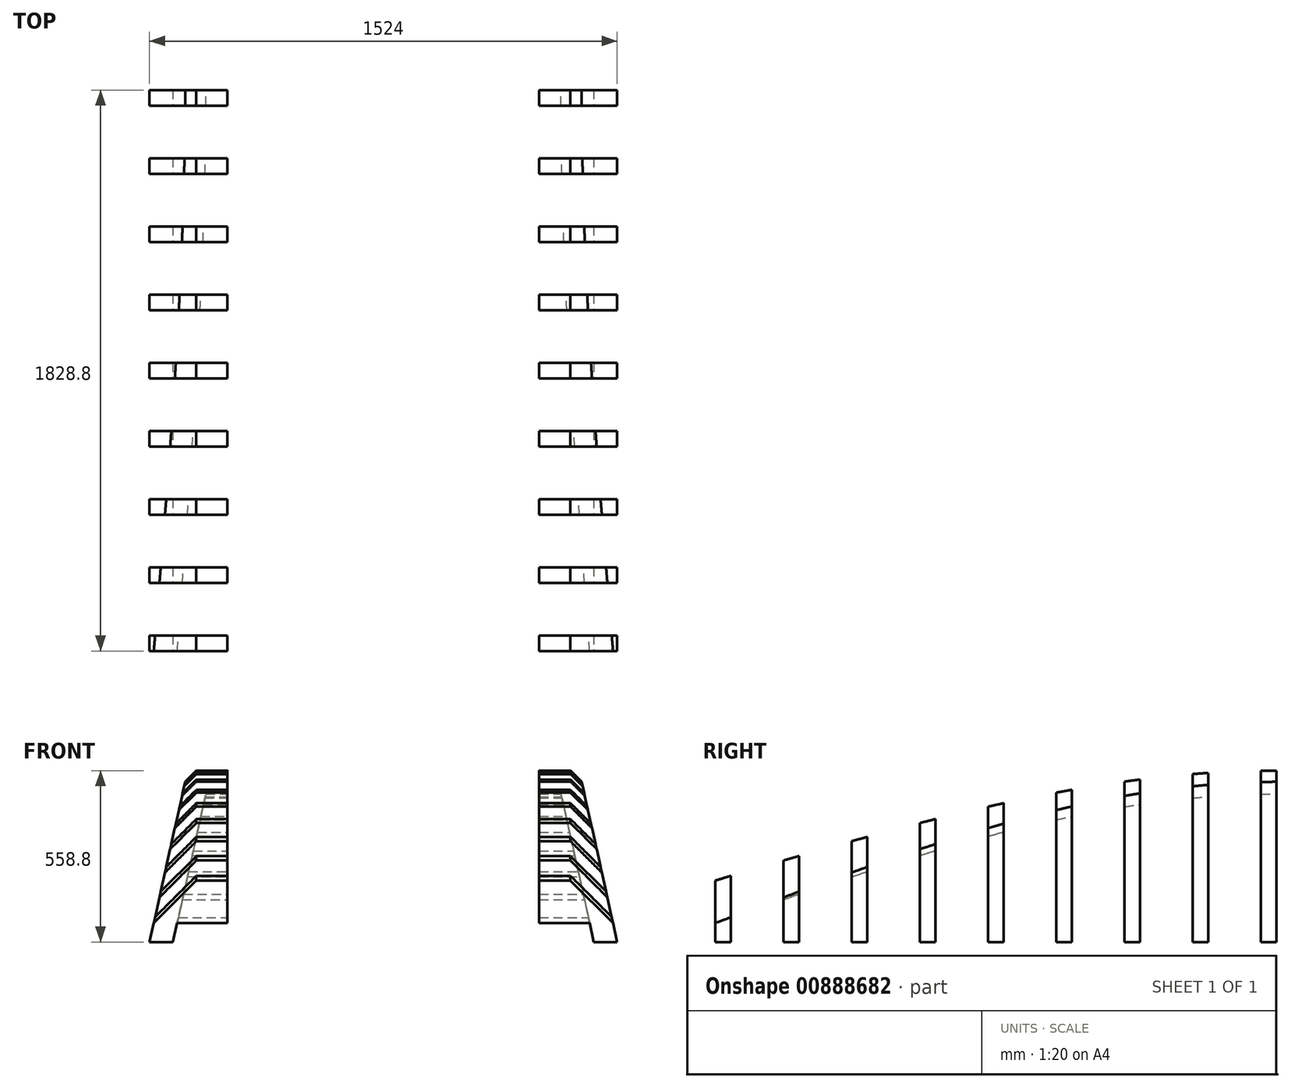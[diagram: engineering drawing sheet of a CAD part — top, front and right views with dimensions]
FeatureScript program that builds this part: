
annotation { "Feature Type Name" : "Feature", "Feature Type Description" : "" }
export const myFeature = defineFeature(function(context is Context, id is Id, definition is map)
    precondition{}
    {
        {
            var Q0;
            Q0=qCreatedBy(makeId("Front.planeOp"),FACE);
            var sketch = newSketch(context, id + "F0", { "sketchPlane" : qUnion([Q0])});
            skLineSegment(sketch, "E0", {"start": v(762, 0) * mm, "end": v(646.24, 522.16) * mm});
            skLineSegment(sketch, "E1", {"start": v(646.24, 522.16) * mm, "end": v(609.6, 558.8) * mm});
            skLineSegment(sketch, "E2", {"start": v(609.6, 558.8) * mm, "end": v(0, 558.8) * mm});
            skLineSegment(sketch, "E3", {"start": v(762, 0) * mm, "end": v(685.8, 0) * mm});
            skLineSegment(sketch, "E4", {"start": v(685.8, 0) * mm, "end": v(578.81, 482.6) * mm});
            skLineSegment(sketch, "E5", {"start": v(578.81, 482.6) * mm, "end": v(0, 482.6) * mm});
            skLineSegment(sketch, "E6", {"start": v(0, 558.8) * mm, "end": v(0, 482.6) * mm, "construction": true});
            skLineSegment(sketch, "E7.MirrorCS", {"start": v(-762, 0) * mm, "end": v(-685.8, 0) * mm});
            skLineSegment(sketch, "E8.MirrorCS", {"start": v(-646.24, 522.16) * mm, "end": v(-609.6, 558.8) * mm});
            skLineSegment(sketch, "E9.MirrorCS", {"start": v(-762, 0) * mm, "end": v(-646.24, 522.16) * mm});
            skLineSegment(sketch, "E10.MirrorCS", {"start": v(-685.8, 0) * mm, "end": v(-578.81, 482.6) * mm});
            skLineSegment(sketch, "E11.MirrorCS", {"start": v(-578.81, 482.6) * mm, "end": v(0, 482.6) * mm});
            skLineSegment(sketch, "E12.MirrorCS", {"start": v(-609.6, 558.8) * mm, "end": v(0, 558.8) * mm});
            skSolve(sketch);
        }
        {
            var Q0;
            Q0=qCreatedBy(makeId("Front.planeOp"),FACE);
            cPlane(context, id + "F1", {"entities" : qUnion([Q0]), "cplaneType" : CPlaneType.OFFSET, "offset" : 1828.8 * mm, "width" : 152.4 * mm, "height" : 152.4 * mm});
        }
        {
            var Q0;
            Q0=qCreatedBy(id+"F1.planeOp",FACE);
            var sketch = newSketch(context, id + "F2", { "sketchPlane" : qUnion([Q0])});
            skLineSegment(sketch, "E13", {"start": v(762, 0) * mm, "end": v(748.26, 62) * mm});
            skLineSegment(sketch, "E14", {"start": v(748.26, 62) * mm, "end": v(609.6, 200.65) * mm});
            skLineSegment(sketch, "E15", {"start": v(609.6, 200.65) * mm, "end": v(0, 200.65) * mm});
            skLineSegment(sketch, "E16", {"start": v(762, 0) * mm, "end": v(685.8, 0) * mm});
            skLineSegment(sketch, "E17", {"start": v(685.8, 0) * mm, "end": v(672.06, 62) * mm});
            skLineSegment(sketch, "E18", {"start": v(672.06, 62) * mm, "end": v(0, 62) * mm});
            skLineSegment(sketch, "E19", {"start": v(0, 62) * mm, "end": v(0, 200.65) * mm, "construction": true});
            skLineSegment(sketch, "E20.MirrorCS", {"start": v(-672.06, 62) * mm, "end": v(0, 62) * mm});
            skLineSegment(sketch, "E21.MirrorCS", {"start": v(-685.8, 0) * mm, "end": v(-672.06, 62) * mm});
            skLineSegment(sketch, "E22.MirrorCS", {"start": v(-609.6, 200.65) * mm, "end": v(0, 200.65) * mm});
            skLineSegment(sketch, "E23.MirrorCS", {"start": v(-748.26, 62) * mm, "end": v(-609.6, 200.65) * mm});
            skLineSegment(sketch, "E24.MirrorCS", {"start": v(-762, 0) * mm, "end": v(-685.8, 0) * mm});
            skLineSegment(sketch, "E25.MirrorCS", {"start": v(-762, 0) * mm, "end": v(-748.26, 62) * mm});
            skSolve(sketch);
        }
        {
            var Q0;
            Q0=makeQuery(id+"F0.imprint","IMPRINT",FACE,{"disambiguationData":[TD([[makeQuery(id+"F0.imprint","IMPRINT",EDGE,{"derivedFrom":sQuery(id+"F0.wireOp",EDGE,"E0")}),1.0]])]});
            var Q1;
            Q1=makeQuery(id+"F2.imprint","IMPRINT",FACE,{"disambiguationData":[TD([[makeQuery(id+"F2.imprint","IMPRINT",EDGE,{"derivedFrom":sQuery(id+"F2.wireOp",EDGE,"E13")}),1.0]])]});
            loft(context, id + "F3", {"sheetProfilesArray" : [{ "sheetProfileEntities" : qUnion([Q0]) }, { "sheetProfileEntities" : qUnion([Q1]) }], "startCondition" : LoftEndDerivativeType.NORMAL_TO_PROFILE, "startMagnitude" : 1});
        }
        {
            var Q0;
            Q0=qCreatedBy(makeId("Right.planeOp"),FACE);
            var sketch = newSketch(context, id + "F4", { "sketchPlane" : qUnion([Q0])});
            skLineSegment(sketch, "E26.bottom", {"start": v(-50.8, 0) * mm, "end": v(-222.25, 0) * mm});
            skLineSegment(sketch, "E26.top", {"start": v(-50.8, 609.6) * mm, "end": v(-222.25, 609.6) * mm});
            skLineSegment(sketch, "E26.left", {"start": v(-50.8, 0) * mm, "end": v(-50.8, 609.6) * mm});
            skLineSegment(sketch, "E26.right", {"start": v(-222.25, 0) * mm, "end": v(-222.25, 609.6) * mm});
            skLineSegment(sketch, "E27.bottom", {"start": v(-273.05, 0) * mm, "end": v(-444.5, 0) * mm});
            skLineSegment(sketch, "E27.top", {"start": v(-273.05, 609.6) * mm, "end": v(-444.5, 609.6) * mm});
            skLineSegment(sketch, "E27.left", {"start": v(-273.05, 0) * mm, "end": v(-273.05, 609.6) * mm});
            skLineSegment(sketch, "E27.right", {"start": v(-444.5, 0) * mm, "end": v(-444.5, 609.6) * mm});
            skLineSegment(sketch, "E28.bottom", {"start": v(-495.3, 0) * mm, "end": v(-666.75, 0) * mm});
            skLineSegment(sketch, "E28.top", {"start": v(-495.3, 609.6) * mm, "end": v(-666.75, 609.6) * mm});
            skLineSegment(sketch, "E28.left", {"start": v(-495.3, 0) * mm, "end": v(-495.3, 609.6) * mm});
            skLineSegment(sketch, "E28.right", {"start": v(-666.75, 0) * mm, "end": v(-666.75, 609.6) * mm});
            skLineSegment(sketch, "E29.bottom", {"start": v(-717.55, 0) * mm, "end": v(-889, 0) * mm});
            skLineSegment(sketch, "E29.top", {"start": v(-717.55, 609.6) * mm, "end": v(-889, 609.6) * mm});
            skLineSegment(sketch, "E29.left", {"start": v(-717.55, 0) * mm, "end": v(-717.55, 609.6) * mm});
            skLineSegment(sketch, "E29.right", {"start": v(-889, 0) * mm, "end": v(-889, 609.6) * mm});
            skLineSegment(sketch, "E30.bottom", {"start": v(-939.8, 0) * mm, "end": v(-1111.25, 0) * mm});
            skLineSegment(sketch, "E30.top", {"start": v(-939.8, 609.6) * mm, "end": v(-1111.25, 609.6) * mm});
            skLineSegment(sketch, "E30.left", {"start": v(-939.8, 0) * mm, "end": v(-939.8, 609.6) * mm});
            skLineSegment(sketch, "E30.right", {"start": v(-1111.25, 0) * mm, "end": v(-1111.25, 609.6) * mm});
            skLineSegment(sketch, "E31.bottom", {"start": v(-1162.05, 0) * mm, "end": v(-1333.5, 0) * mm});
            skLineSegment(sketch, "E31.top", {"start": v(-1162.05, 609.6) * mm, "end": v(-1333.5, 609.6) * mm});
            skLineSegment(sketch, "E31.left", {"start": v(-1162.05, 0) * mm, "end": v(-1162.05, 609.6) * mm});
            skLineSegment(sketch, "E31.right", {"start": v(-1333.5, 0) * mm, "end": v(-1333.5, 609.6) * mm});
            skLineSegment(sketch, "E32.bottom", {"start": v(-50.8, 0) * mm, "end": v(0, 0) * mm});
            skLineSegment(sketch, "E32.top", {"start": v(-50.8, 0) * mm, "end": v(0, 0) * mm});
            skLineSegment(sketch, "E32.left", {"start": v(-50.8, 0) * mm, "end": v(-50.8, 0) * mm});
            skLineSegment(sketch, "E32.right", {"start": v(0, 0) * mm, "end": v(0, 0) * mm});
            skLineSegment(sketch, "E33.bottom", {"start": v(-1384.3, 0) * mm, "end": v(-1555.75, 0) * mm});
            skLineSegment(sketch, "E33.top", {"start": v(-1384.3, 609.6) * mm, "end": v(-1555.75, 609.6) * mm});
            skLineSegment(sketch, "E33.left", {"start": v(-1384.3, 0) * mm, "end": v(-1384.3, 609.6) * mm});
            skLineSegment(sketch, "E33.right", {"start": v(-1555.75, 0) * mm, "end": v(-1555.75, 609.6) * mm});
            skLineSegment(sketch, "E34.bottom", {"start": v(-1606.55, 0) * mm, "end": v(-1778, 0) * mm});
            skLineSegment(sketch, "E34.top", {"start": v(-1606.55, 609.6) * mm, "end": v(-1778, 609.6) * mm});
            skLineSegment(sketch, "E34.left", {"start": v(-1606.55, 0) * mm, "end": v(-1606.55, 609.6) * mm});
            skLineSegment(sketch, "E34.right", {"start": v(-1778, 0) * mm, "end": v(-1778, 609.6) * mm});
            skSolve(sketch);
        }
        {
            var Q0;
            Q0 = qSketchRegion(id + "F4", true);
            extrude(context, id + "F5", {"entities" : qUnion([Q0]), "operationType" : NewBodyOperationType.REMOVE, "endBound" : BoundingType.SYMMETRIC, "oppositeDirection" : true, "depth" : 1524 * mm, "offsetDistance" : 25.4 * mm});
        }
        {
            var Q0;
            Q0=qCreatedBy(makeId("Top.planeOp"),FACE);
            var sketch = newSketch(context, id + "F6", { "sketchPlane" : qUnion([Q0])});
            skLineSegment(sketch, "E35.bottom", {"start": v(-508, 0) * mm, "end": v(508, 0) * mm});
            skLineSegment(sketch, "E35.top", {"start": v(-508, -1828.8) * mm, "end": v(508, -1828.8) * mm});
            skLineSegment(sketch, "E35.left", {"start": v(-508, 0) * mm, "end": v(-508, -1828.8) * mm});
            skLineSegment(sketch, "E35.right", {"start": v(508, 0) * mm, "end": v(508, -1828.8) * mm});
            skSolve(sketch);
        }
        {
            var Q0;
            Q0 = qSketchRegion(id + "F6", true);
            var Q1;
            {var subQ0=sQuery(id+"F2.wireOp",EDGE,"E15");var subQ1=sQuery(id+"F2.wireOp",EDGE,"E14");var subQ2=sQuery(id+"F0.wireOp",EDGE,"E2");var subQ3=sQuery(id+"F0.wireOp",EDGE,"E1");var subQ5=sQuery(id+"F2.wireOp",EDGE,"E23.MirrorCS");var subQ6=sQuery(id+"F2.wireOp",EDGE,"E22.MirrorCS");var subQ7=sQuery(id+"F0.wireOp",EDGE,"E12.MirrorCS");var subQ9=sQuery(id+"F0.wireOp",EDGE,"E8.MirrorCS");Q1=makeQuery(id+"F5.boolean.opBoolean","SPLIT",FACE,{"disambiguationData":[TD([makeQuery(id+"F5.opExtrude","SWEPT_FACE",FACE,{"disambiguationData":[OSD([sQuery(id+"F4.wireOp",EDGE,"E26.left")])]})])],"derivedFrom":makeQuery(id+"F3.opLoft","SWEPT_FACE",FACE,{"disambiguationData":[OSD([subQ3,subQ2,subQ9,subQ7,subQ1,subQ0,subQ6,subQ5])]})});}
            extrude(context, id + "F7", {"entities" : qUnion([Q0]), "operationType" : NewBodyOperationType.REMOVE, "depth" : 635 * mm, "endBoundEntityFace" : qUnion([Q1]), "offsetDistance" : 25.4 * mm});
        }
    });
